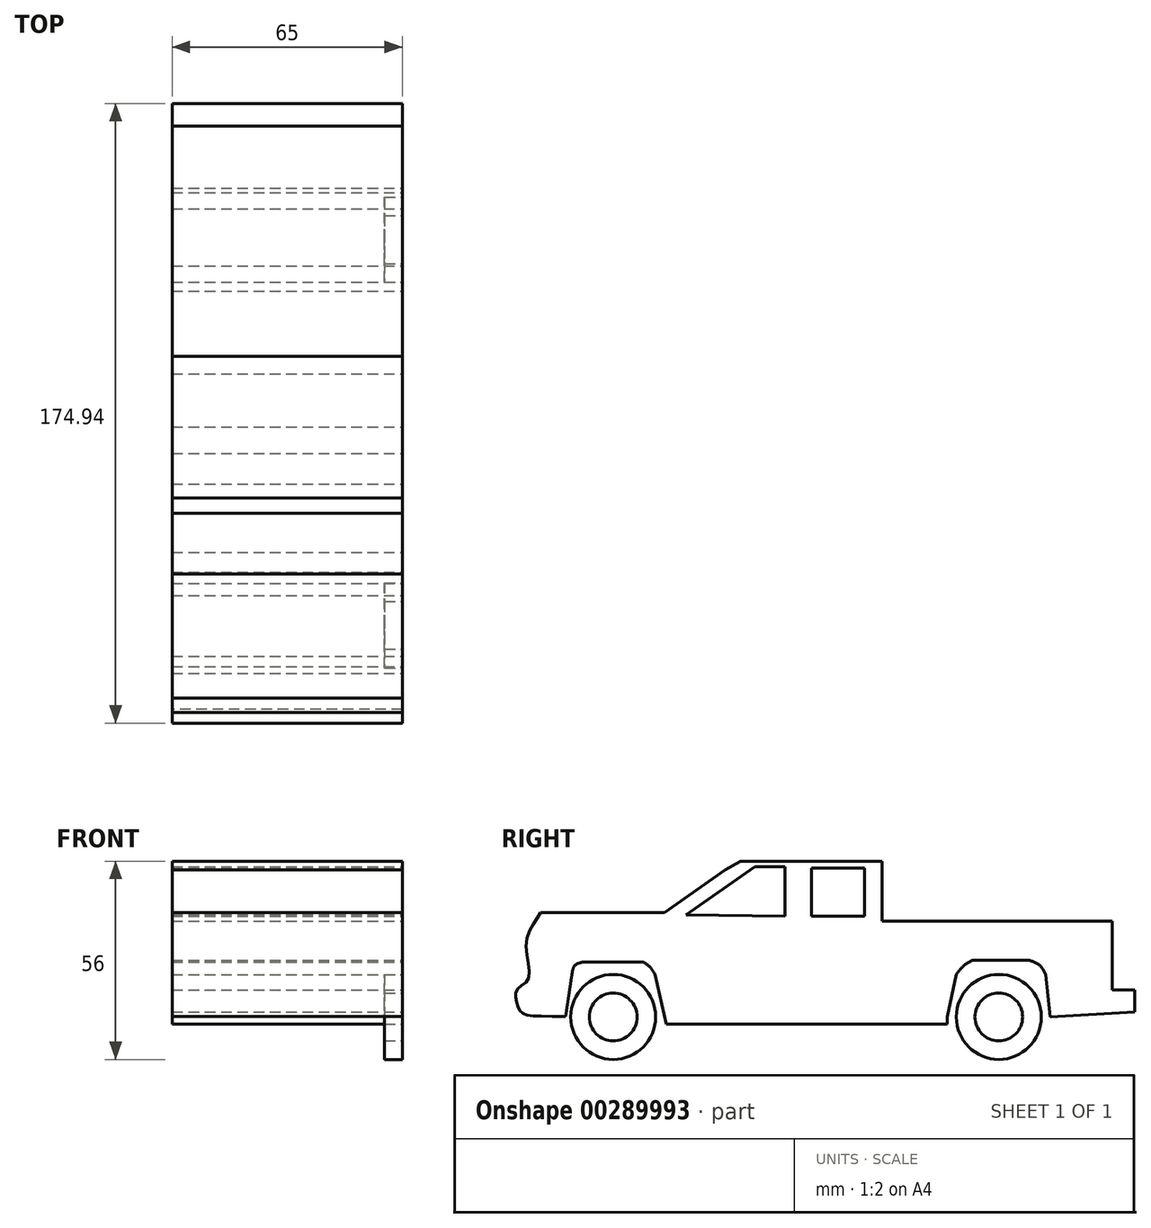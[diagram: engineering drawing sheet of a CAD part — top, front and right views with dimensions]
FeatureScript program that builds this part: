
annotation { "Feature Type Name" : "Feature", "Feature Type Description" : "" }
export const myFeature = defineFeature(function(context is Context, id is Id, definition is map)
    precondition{}
    {
        {
            var Q0;
            Q0=qCreatedBy(makeId("Right.planeOp"),FACE);
            var sketch = newSketch(context, id + "F0", { "sketchPlane" : qUnion([Q0])});
            skLineSegment(sketch, "E0", {"start": v(-51.38, 19.36) * mm, "end": v(13.62, 19.36) * mm});
            skLineSegment(sketch, "E1", {"start": v(-51.38, 19.36) * mm, "end": v(-51.38, 36.36) * mm});
            skLineSegment(sketch, "E2", {"start": v(-51.38, 36.36) * mm, "end": v(-91.38, 36.36) * mm});
            skLineSegment(sketch, "E3", {"start": v(-91.38, 36.36) * mm, "end": v(-95.71, 33.86) * mm});
            skLineSegment(sketch, "E4", {"start": v(-95.71, 33.86) * mm, "end": v(-112.92, 21.82) * mm});
            skLineSegment(sketch, "E5", {"start": v(-112.92, 21.82) * mm, "end": v(-147.92, 21.82) * mm});
            skLineSegment(sketch, "E6", {"start": v(-73.38, 36.36) * mm, "end": v(-73.38, -7.64) * mm});
            skLineSegment(sketch, "E7", {"start": v(-54.38, 36.36) * mm, "end": v(-54.38, -7.64) * mm});
            skLineSegment(sketch, "E8", {"start": v(-73.38, -7.64) * mm, "end": v(-108.38, -7.64) * mm});
            skLineSegment(sketch, "E9", {"start": v(-73.38, -7.64) * mm, "end": v(-54.38, -7.64) * mm});
            skLineSegment(sketch, "E10", {"start": v(-54.38, -7.64) * mm, "end": v(-37.38, -7.64) * mm});
            skLineSegment(sketch, "E11", {"start": v(-51.38, 19.36) * mm, "end": v(-51.38, -7.64) * mm});
            skLineSegment(sketch, "E12.0", {"start": v(-50.38, 18.36) * mm, "end": v(12.6, 18.36) * mm});
            skLineSegment(sketch, "E12.1", {"start": v(-50.38, 18.36) * mm, "end": v(-50.38, -7.64) * mm});
            skLineSegment(sketch, "E13", {"start": v(-73.38, -7.64) * mm, "end": v(-127.38, -7.64) * mm, "construction": true});
            skCircle(sketch, "E14", {"center": v(-18.46, -7.64) * mm, "radius": 12 * mm});
            skCircle(sketch, "E15", {"center": v(-127.38, -7.64) * mm, "radius": 12 * mm});
            skCircle(sketch, "E16", {"center": v(-18.46, -7.64) * mm, "radius": 10.5 * mm});
            skCircle(sketch, "E17", {"center": v(-127.38, -7.64) * mm, "radius": 10.5 * mm});
            skCircle(sketch, "E18", {"center": v(-18.46, -7.64) * mm, "radius": 6.75 * mm});
            skCircle(sketch, "E19", {"center": v(-127.38, -7.64) * mm, "radius": 6.75 * mm});
            skLineSegment(sketch, "E20", {"start": v(-73.38, -7.64) * mm, "end": v(-73.38, -9.64) * mm, "construction": true});
            skLineSegment(sketch, "E21", {"start": v(-73.38, -9.64) * mm, "end": v(-32.96, -9.64) * mm});
            skLineSegment(sketch, "E22", {"start": v(-73.38, -9.64) * mm, "end": v(-112.38, -9.64) * mm});
            skLineSegment(sketch, "E23", {"start": v(-106.77, 21.24) * mm, "end": v(-87.42, 34.78) * mm});
            skLineSegment(sketch, "E24", {"start": v(-54.38, 32.9) * mm, "end": v(-54.38, 21.24) * mm});
            skLineSegment(sketch, "E25", {"start": v(-87.42, 34.78) * mm, "end": v(-78.87, 34.78) * mm});
            skLineSegment(sketch, "E26", {"start": v(-78.87, 34.78) * mm, "end": v(-78.87, 20.8) * mm});
            skLineSegment(sketch, "E27", {"start": v(-78.87, 20.8) * mm, "end": v(-106.77, 21.24) * mm});
            skFitSpline(sketch, "E28", {"points": [v(-147.92, 21.82) * mm, v(-151.9, 13.53) * mm, v(-151.45, 3.07) * mm, v(-154.6, 0) * mm, v(-154.6, -3.68) * mm, v(-153.05, -6.54) * mm, v(-139.38, -7.64) * mm], "startDerivative": vector(-19.35, -33.45) * mm, "endDerivative": vector(106.71, -6.3) * mm});
            skLineSegment(sketch, "E29", {"start": v(-108.38, -7.64) * mm, "end": v(-108.38, 22.55) * mm});
            skLineSegment(sketch, "E30", {"start": v(-112.92, 21.82) * mm, "end": v(-108.38, 22.55) * mm});
            skLineSegment(sketch, "E31", {"start": v(-108.38, 22.55) * mm, "end": v(-90.1, 35.34) * mm});
            skLineSegment(sketch, "E32", {"start": v(-90.1, 35.34) * mm, "end": v(-93.16, 35.34) * mm});
            skPoint(sketch, "E32.endSnap0", {"position": v(-93.55, 35.11) * mm});
            skPoint(sketch, "E33.orphan", {"position": v(-93.55, 35.34) * mm});
            skLineSegment(sketch, "E34.0", {"start": v(-79.87, 33.78) * mm, "end": v(-79.87, 21.81) * mm});
            skLineSegment(sketch, "E35.0", {"start": v(-87.42, 33.78) * mm, "end": v(-78.87, 33.78) * mm});
            skLineSegment(sketch, "E36.0", {"start": v(-78.86, 21.8) * mm, "end": v(-78.87, 21.8) * mm});
            skLineSegment(sketch, "E37.trimOffspring", {"start": v(-79.87, 20.81) * mm, "end": v(-79.87, 20.8) * mm});
            skLineSegment(sketch, "E38.trimOffspring", {"start": v(-79.87, 21.81) * mm, "end": v(-103.66, 22.19) * mm});
            skLineSegment(sketch, "E39.trimOffspring", {"start": v(-103.66, 22.19) * mm, "end": v(-86.85, 33.96) * mm});
            skPoint(sketch, "E40.endSnap0", {"position": v(-71.38, 36.36) * mm});
            skLineSegment(sketch, "E41", {"start": v(-73.38, 36.36) * mm, "end": v(-54.38, 36.36) * mm});
            skLineSegment(sketch, "E42", {"start": v(-73.38, 20.8) * mm, "end": v(-73.38, 36.36) * mm});
            skLineSegment(sketch, "E43", {"start": v(-73.38, 36.36) * mm, "end": v(-73.38, 20.8) * mm});
            skLineSegment(sketch, "E44", {"start": v(-54.38, 20.8) * mm, "end": v(-54.38, 36.36) * mm});
            skLineSegment(sketch, "E45.0", {"start": v(-71.38, 34.36) * mm, "end": v(-71.38, 20.8) * mm});
            skLineSegment(sketch, "E45.1", {"start": v(-71.38, 34.36) * mm, "end": v(-56.38, 34.36) * mm});
            skLineSegment(sketch, "E45.2", {"start": v(-56.38, 20.8) * mm, "end": v(-56.38, 34.36) * mm});
            skLineSegment(sketch, "E46", {"start": v(-71.38, 20.8) * mm, "end": v(-56.38, 20.8) * mm});
            skLineSegment(sketch, "E47.0", {"start": v(-70.38, 33.36) * mm, "end": v(-57.38, 33.36) * mm});
            skLineSegment(sketch, "E47.1", {"start": v(-70.38, 33.36) * mm, "end": v(-70.38, 21.8) * mm});
            skLineSegment(sketch, "E47.2", {"start": v(-70.38, 21.8) * mm, "end": v(-57.38, 21.8) * mm});
            skLineSegment(sketch, "E47.3", {"start": v(-57.38, 21.8) * mm, "end": v(-57.38, 33.36) * mm});
            skLineSegment(sketch, "E48", {"start": v(-18.29, 4.36) * mm, "end": v(-18.29, 8.36) * mm, "construction": true});
            skLineSegment(sketch, "E49", {"start": v(-3.96, -7.66) * mm, "end": v(-5.17, 4.36) * mm});
            skLineSegment(sketch, "E50", {"start": v(-32.96, -7.64) * mm, "end": v(-30.46, 4.36) * mm});
            skLineSegment(sketch, "E51", {"start": v(-18.29, 8.36) * mm, "end": v(-9.74, 8.36) * mm});
            skLineSegment(sketch, "E52", {"start": v(-18.29, 8.36) * mm, "end": v(-25.91, 8.36) * mm});
            skFitSpline(sketch, "E53", {"points": [v(-25.91, 8.36) * mm, v(-28.28, 6.9) * mm, v(-30.46, 4.36) * mm], "startDerivative": vector(-5.17, -2.61) * mm, "endDerivative": vector(-3.94, -5.34) * mm});
            skFitSpline(sketch, "E54", {"points": [v(-9.74, 8.36) * mm, v(-7, 7.05) * mm, v(-5.17, 4.36) * mm], "startDerivative": vector(6.07, -2.02) * mm, "endDerivative": vector(3.1, -5.96) * mm});
            skLineSegment(sketch, "E55", {"start": v(-37.38, -7.64) * mm, "end": v(-32.96, -7.64) * mm});
            skLineSegment(sketch, "E56", {"start": v(-32.96, -7.64) * mm, "end": v(-32.96, -9.64) * mm});
            skPoint(sketch, "E57.orphan", {"position": v(-30.46, -9.64) * mm});
            skLineSegment(sketch, "E58", {"start": v(-127.05, 4.36) * mm, "end": v(-127.05, 7.86) * mm, "construction": true});
            skLineSegment(sketch, "E59", {"start": v(-139.38, -7.64) * mm, "end": v(-140.88, -7.56) * mm, "construction": true});
            skLineSegment(sketch, "E60", {"start": v(-140.88, -7.56) * mm, "end": v(-139.05, 4.36) * mm});
            skLineSegment(sketch, "E61", {"start": v(-112.38, -9.64) * mm, "end": v(-115.5, 4.36) * mm});
            skLineSegment(sketch, "E62", {"start": v(-127.05, 7.86) * mm, "end": v(-118.95, 7.86) * mm});
            skLineSegment(sketch, "E63", {"start": v(-127.05, 7.86) * mm, "end": v(-136.14, 7.86) * mm});
            skFitSpline(sketch, "E64", {"points": [v(-136.14, 7.86) * mm, v(-138.27, 6.87) * mm, v(-139.05, 4.36) * mm], "startDerivative": vector(-5.1, -1.33) * mm, "endDerivative": vector(-0.76, -5.63) * mm});
            skFitSpline(sketch, "E65", {"points": [v(-115.5, 4.36) * mm, v(-117.18, 6.66) * mm, v(-118.95, 7.86) * mm], "startDerivative": vector(-2.94, 4.75) * mm, "endDerivative": vector(-3.97, 2.19) * mm});
            skLineSegment(sketch, "E66", {"start": v(13.62, 19.36) * mm, "end": v(13.62, 16.62) * mm});
            skLineSegment(sketch, "E67", {"start": v(13.62, 16.62) * mm, "end": v(13.62, 5.81) * mm});
            skLineSegment(sketch, "E68", {"start": v(13.62, 5.81) * mm, "end": v(13.62, 0) * mm});
            skLineSegment(sketch, "E69", {"start": v(13.62, 0) * mm, "end": v(19.96, 0) * mm});
            skLineSegment(sketch, "E70", {"start": v(19.96, 0) * mm, "end": v(19.96, -6.18) * mm});
            skLineSegment(sketch, "E71", {"start": v(19.96, -6.18) * mm, "end": v(-3.96, -7.66) * mm});
            skSolve(sketch);
        }
        {
            var Q0;
            Q0=makeQuery(id+"F0.imprint","IMPRINT",FACE,{"disambiguationData":[TD([[makeQuery(id+"F0.imprint","IMPRINT",EDGE,{"derivedFrom":sQuery(id+"F0.wireOp",EDGE,"E0")}),-1.0]])]});
            var Q1;
            {var subQ5=sQuery(id+"F0.wireOp",EDGE,"E1");Q1=makeQuery(id+"F0.imprint","IMPRINT",FACE,{"disambiguationData":[TD([[makeQuery(id+"F0.imprint","IMPRINT",EDGE,{"derivedFrom":subQ5}),1.0]])]});}
            var Q2;
            Q2=makeQuery(id+"F0.imprint","IMPRINT",FACE,{"disambiguationData":[TD([[makeQuery(id+"F0.imprint","IMPRINT",EDGE,{"derivedFrom":sQuery(id+"F0.wireOp",EDGE,"E6")}),1.0]])]});
            var Q3;
            Q3=makeQuery(id+"F0.imprint","IMPRINT",FACE,{"disambiguationData":[TD([[makeQuery(id+"F0.imprint","IMPRINT",EDGE,{"derivedFrom":sQuery(id+"F0.wireOp",EDGE,"E6")}),-1.0]])]});
            var Q4;
            {var subQ0=sQuery(id+"F0.wireOp",EDGE,"E4");Q4=makeQuery(id+"F0.imprint","IMPRINT",FACE,{"disambiguationData":[TD([[makeQuery(id+"F0.imprint","IMPRINT",EDGE,{"derivedFrom":subQ0}),1.0]])]});}
            var Q5;
            {var subQ1=sQuery(id+"F0.wireOp",EDGE,"E5");Q5=makeQuery(id+"F0.imprint","IMPRINT",FACE,{"disambiguationData":[TD([[makeQuery(id+"F0.imprint","IMPRINT",EDGE,{"derivedFrom":subQ1}),1.0]])]});}
            extrude(context, id + "F1", {"entities" : qUnion([Q0, Q1, Q2, Q3, Q4, Q5]), "oppositeDirection" : true, "depth" : 65 * mm});
        }
        {
            var Q0;
            Q0=makeQuery(id+"F0.imprint","IMPRINT",FACE,{"disambiguationData":[TD([[makeQuery(id+"F0.imprint","IMPRINT",EDGE,{"derivedFrom":sQuery(id+"F0.wireOp",EDGE,"E15")}),1.0]])]});
            var Q1;
            Q1=makeQuery(id+"F0.imprint","IMPRINT",FACE,{"disambiguationData":[TD([[makeQuery(id+"F0.imprint","IMPRINT",EDGE,{"derivedFrom":sQuery(id+"F0.wireOp",EDGE,"E17")}),1.0]])]});
            extrude(context, id + "F2", {"entities" : qUnion([Q0, Q1]), "oppositeDirection" : true, "depth" : 5 * mm});
        }
        {
            var Q0;
            Q0=makeQuery(id+"F0.imprint","IMPRINT",FACE,{"disambiguationData":[TD([[makeQuery(id+"F0.imprint","IMPRINT",EDGE,{"derivedFrom":sQuery(id+"F0.wireOp",EDGE,"E14")}),1.0]])]});
            var Q1;
            Q1=makeQuery(id+"F0.imprint","IMPRINT",FACE,{"disambiguationData":[TD([[makeQuery(id+"F0.imprint","IMPRINT",EDGE,{"derivedFrom":sQuery(id+"F0.wireOp",EDGE,"E16")}),1.0]])]});
            extrude(context, id + "F3", {"entities" : qUnion([Q0, Q1]), "oppositeDirection" : true, "depth" : 5 * mm});
        }
    });
